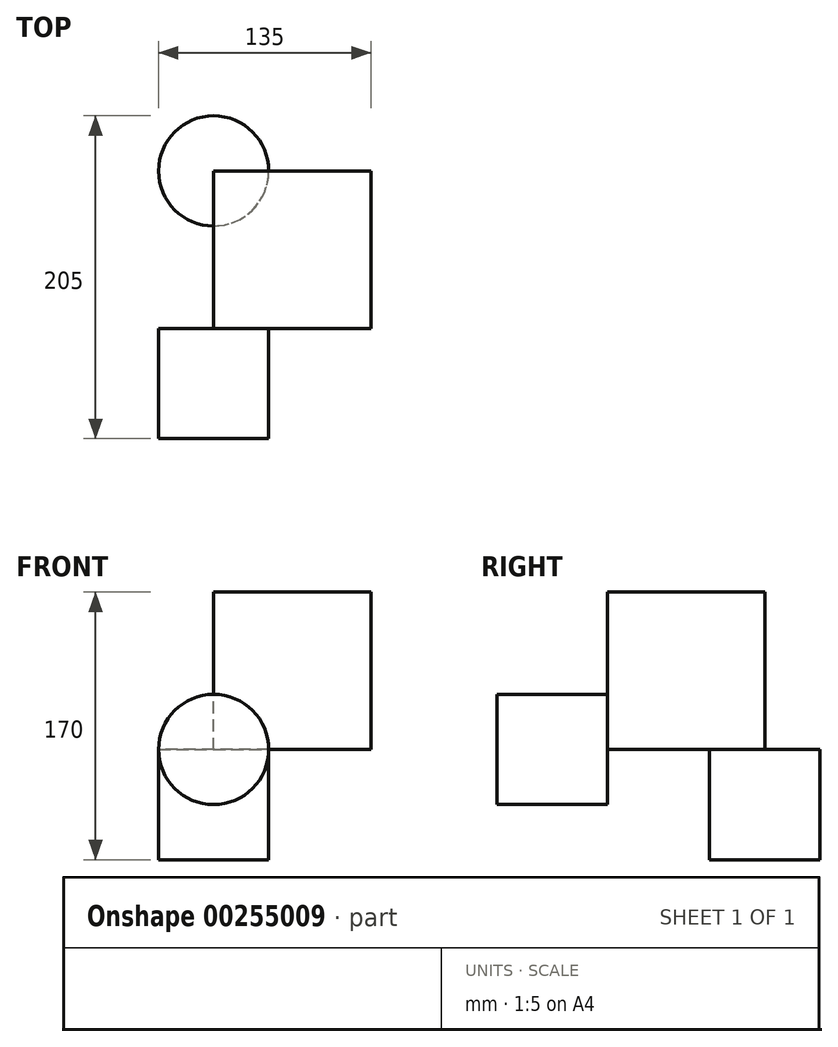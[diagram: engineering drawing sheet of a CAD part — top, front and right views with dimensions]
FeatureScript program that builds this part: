
annotation { "Feature Type Name" : "Feature", "Feature Type Description" : "" }
export const myFeature = defineFeature(function(context is Context, id is Id, definition is map)
    precondition{}
    {
        {
            var Q0;
            Q0=qCreatedBy(makeId("Front.planeOp"),FACE);
            var sketch = newSketch(context, id + "F0", { "sketchPlane" : qUnion([Q0])});
            skLineSegment(sketch, "E0.bottom", {"start": v(0, 0) * mm, "end": v(100, 0) * mm});
            skLineSegment(sketch, "E0.top", {"start": v(0, 100) * mm, "end": v(100, 100) * mm});
            skLineSegment(sketch, "E0.left", {"start": v(0, 0) * mm, "end": v(0, 100) * mm});
            skLineSegment(sketch, "E0.right", {"start": v(100, 0) * mm, "end": v(100, 100) * mm});
            skSolve(sketch);
        }
        {
            var Q0;
            Q0 = qSketchRegion(id + "F0", true);
            extrude(context, id + "F1", {"entities" : qUnion([Q0]), "depth" : 100 * mm});
        }
        {
            var Q0;
            Q0=makeQuery(id+"F1.opExtrude","CAP_FACE",FACE,{"disambiguationData":[OSD([sQuery(id+"F0.wireOp",EDGE,"E0.bottom"),sQuery(id+"F0.wireOp",EDGE,"E0.top"),sQuery(id+"F0.wireOp",EDGE,"E0.left"),sQuery(id+"F0.wireOp",EDGE,"E0.right")])],"isStart":false});
            var sketch = newSketch(context, id + "F2", { "sketchPlane" : qUnion([Q0])});
            skCircle(sketch, "E1", {"center": v(0, 0) * mm, "radius": 35 * mm});
            skSolve(sketch);
        }
        {
            var Q0;
            Q0 = qSketchRegion(id + "F2", true);
            extrude(context, id + "F3", {"entities" : qUnion([Q0]), "operationType" : NewBodyOperationType.ADD, "depth" : 70 * mm});
        }
        {
            var Q0;
            Q0=makeQuery(id+"F1.opExtrude","SWEPT_FACE",FACE,{"disambiguationData":[OSD([sQuery(id+"F0.wireOp",EDGE,"E0.bottom")])]});
            var sketch = newSketch(context, id + "F4", { "sketchPlane" : qUnion([Q0])});
            skCircle(sketch, "E2", {"center": v(0, 0) * mm, "radius": 35 * mm});
            skSolve(sketch);
        }
        {
            var Q0;
            Q0 = qSketchRegion(id + "F4", true);
            extrude(context, id + "F5", {"entities" : qUnion([Q0]), "operationType" : NewBodyOperationType.ADD, "depth" : 70 * mm});
        }
    });
